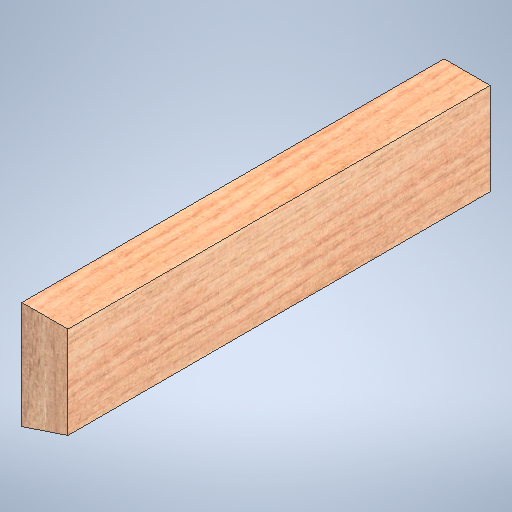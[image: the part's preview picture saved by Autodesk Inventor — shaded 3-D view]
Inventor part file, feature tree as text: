
AUTODESK INVENTOR PART (.ipt)
format: ipt  version: 2025 (Build 290162010, 162A)  size: 413,184 bytes
history: native  units: in
note: dims shown in document units (in); Inventor stores cm internally (conversion verified against a paired STEP export)
features: extrude x1, sketch x1
ambient origin geometry x8: Origin, YZ Plane, XZ Plane, XY Plane, X Axis, Y Axis, Z Axis, Center Point
bodies: Body1 (feature_tree)
feature tree (2):
  extrude  "Extrusion2"  Depth=13.75in
  sketch  "Sketch1"  dims[d33=42.875in d36=132.0in d37=3.5in d38=3.5in d39=1.5in d40=13.75in d41=0.0in]
